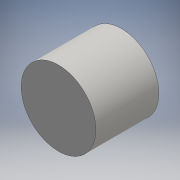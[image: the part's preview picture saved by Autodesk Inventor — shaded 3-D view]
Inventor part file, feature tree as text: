
AUTODESK INVENTOR PART (.ipt)
format: ipt  version: 2016 (Build 200138000, 138)  size: 87,552 bytes
history: native  units: mm
features: other x1, extrude x1, sketch x1
ambient origin geometry x8: Origin, YZ Plane, XZ Plane, XY Plane, X Axis, Y Axis, Z Axis, Center Point
bodies: Body1 (feature_tree)
feature tree (3):
  other  "ソリッド1"
  extrude  "押し出し1"  Depth=38.0mm
  sketch  "スケッチ1"
